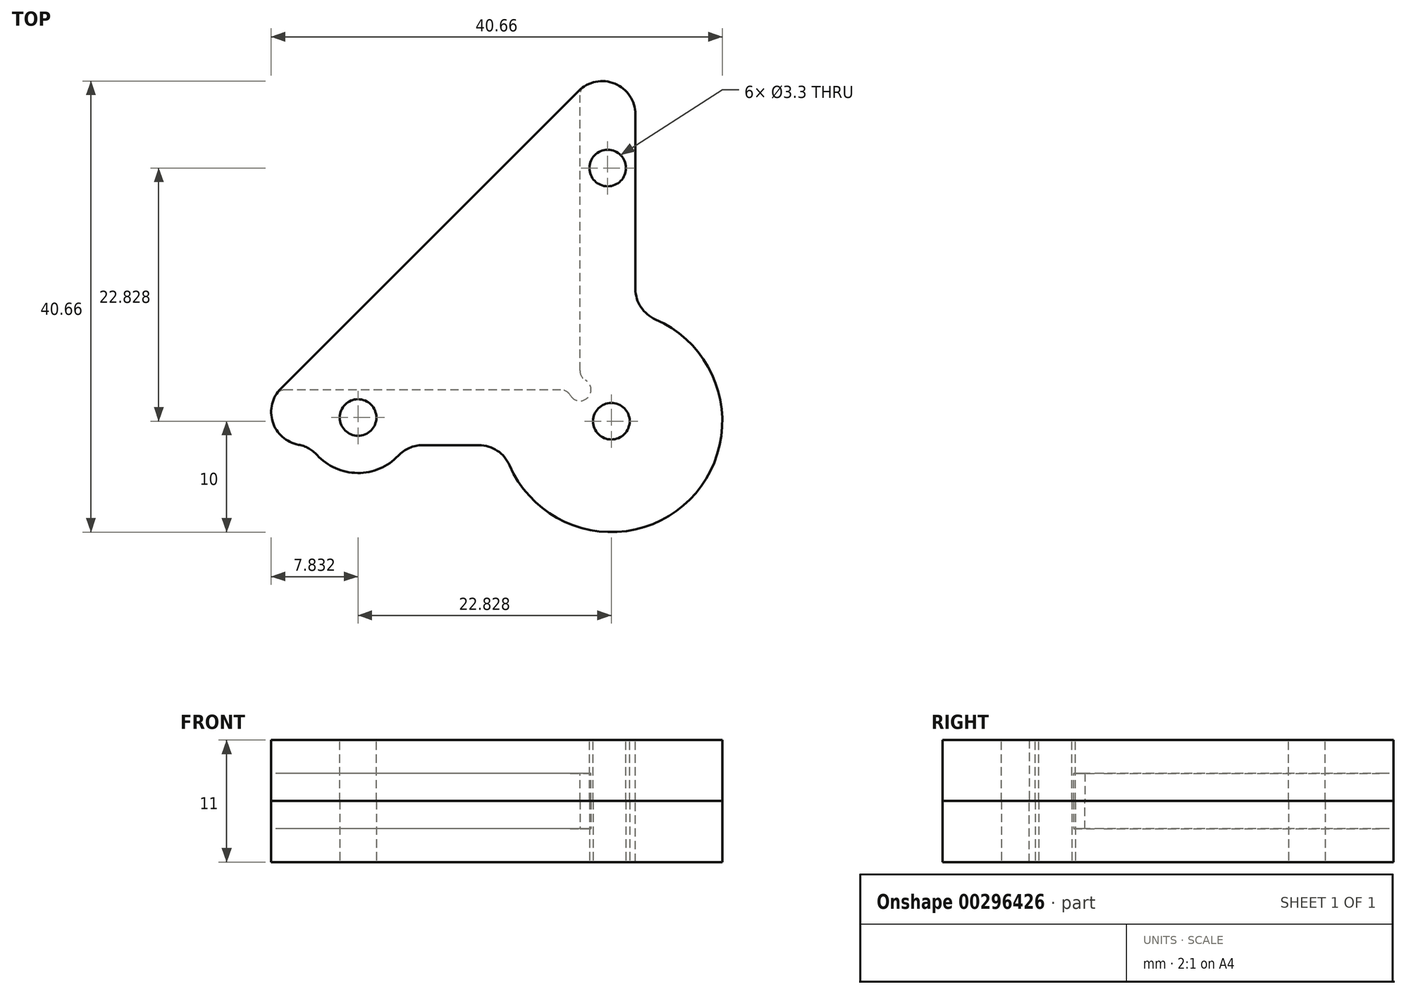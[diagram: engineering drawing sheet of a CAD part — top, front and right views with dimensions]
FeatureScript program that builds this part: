
annotation { "Feature Type Name" : "Feature", "Feature Type Description" : "" }
export const myFeature = defineFeature(function(context is Context, id is Id, definition is map)
    precondition{}
    {
        {
            var Q0;
            Q0=qCreatedBy(makeId("Top.planeOp"),FACE);
            var sketch = newSketch(context, id + "F0", { "sketchPlane" : qUnion([Q0])});
            skCircle(sketch, "E0", {"center": v(0, 0) * mm, "radius": 10 * mm});
            skCircle(sketch, "E1", {"center": v(0, 0) * mm, "radius": 1.65 * mm});
            skLineSegment(sketch, "E2", {"start": v(-2.83, 22.83) * mm, "end": v(2.17, 22.83) * mm, "construction": true});
            skLineSegment(sketch, "E3", {"start": v(-22.83, 2.83) * mm, "end": v(-22.83, -2.17) * mm, "construction": true});
            skPoint(sketch, "E4", {"position": v(-0.33, 22.83) * mm});
            skPoint(sketch, "E5", {"position": v(-22.83, 0.33) * mm});
            skCircle(sketch, "E6", {"center": v(-0.33, 22.83) * mm, "radius": 1.65 * mm});
            skCircle(sketch, "E7", {"center": v(-22.83, 0.33) * mm, "radius": 1.65 * mm});
            skLineSegment(sketch, "E8", {"start": v(0, 0) * mm, "end": v(-31.82, 31.82) * mm, "construction": true});
            skLineSegment(sketch, "E9", {"start": v(-2.83, 2.83) * mm, "end": v(-22.83, 2.83) * mm});
            skLineSegment(sketch, "E10", {"start": v(-2.83, 2.83) * mm, "end": v(-2.83, 22.83) * mm});
            skLineSegment(sketch, "E11", {"start": v(-22.83, 2.83) * mm, "end": v(-2.83, 22.83) * mm});
            skCircle(sketch, "E12", {"center": v(-2.83, 2.83) * mm, "radius": 1 * mm});
            skLineSegment(sketch, "E13", {"start": v(2.17, 9.76) * mm, "end": v(2.17, 34.9) * mm});
            skLineSegment(sketch, "E14", {"start": v(2.17, 34.9) * mm, "end": v(-34.9, -2.17) * mm});
            skLineSegment(sketch, "E15", {"start": v(-34.9, -2.17) * mm, "end": v(-9.76, -2.17) * mm});
            skLineSegment(sketch, "E16", {"start": v(-2.83, 22.83) * mm, "end": v(-2.83, 29.9) * mm});
            skLineSegment(sketch, "E17", {"start": v(-22.83, 2.83) * mm, "end": v(-29.9, 2.83) * mm});
            skArc(sketch, "E18", {"start": v(-27.16, -2.17) * mm, "mid": v(-22.83, -4.67) * mm, "end": v(-18.5, -2.17) * mm});
            skArc(sketch, "E19.MirrorCS", {"start": v(2.17, 27.16) * mm, "mid": v(4.67, 22.83) * mm, "end": v(2.17, 18.5) * mm});
            skSolve(sketch);
        }
        {
            var Q0;
            {var subQ5=sQuery(id+"F0.wireOp",EDGE,"Az8r9AQi-yTUi-chnx-iCbM-hz0Is2fI5o3N");Q0=makeQuery(id+"F0.imprint","IMPRINT",FACE,{"disambiguationData":[TD([[makeQuery(id+"F0.imprint","IMPRINT",EDGE,{"derivedFrom":subQ5}),-1.0]])]});}
            var Q1;
            Q1=makeQuery(id+"F0.imprint","IMPRINT",FACE,{"disambiguationData":[TD([[makeQuery(id+"F0.imprint","IMPRINT",EDGE,{"derivedFrom":sQuery(id+"F0.wireOp",EDGE,"Az8r9AQi-yTUi-chnx-iCbM-hz0Is2fI5o3N")}),1.0]])]});
            var Q2;
            {var subQ5=sQuery(id+"F0.wireOp",EDGE,"E11");Q2=makeQuery(id+"F0.imprint","IMPRINT",FACE,{"disambiguationData":[TD([[makeQuery(id+"F0.imprint","IMPRINT",EDGE,{"derivedFrom":subQ5}),-1.0]])]});}
            var Q3;
            {var subQ0=sQuery(id+"F0.wireOp",EDGE,"E10");var subQ1=sQuery(id+"F0.wireOp",EDGE,"E0");var subQ2=makeQuery(id+"F0.imprint","INTERSECT",VERTEX,{"derivedFrom":[subQ1,subQ0]});Q3=makeQuery(id+"F0.imprint","IMPRINT",FACE,{"disambiguationData":[TD([[makeQuery(id+"F0.imprint","IMPRINT",EDGE,{"disambiguationData":[TD([[subQ2,-1.0]])],"derivedFrom":subQ1}),1.0]])]});}
            var Q4;
            Q4=makeQuery(id+"F0.imprint","IMPRINT",FACE,{"disambiguationData":[TD([[makeQuery(id+"F0.imprint","IMPRINT",EDGE,{"derivedFrom":sQuery(id+"F0.wireOp",EDGE,"E11")}),1.0]])]});
            var Q5;
            {var subQ0=sQuery(id+"F0.wireOp",EDGE,"E10");var subQ1=sQuery(id+"F0.wireOp",EDGE,"E9");var subQ2=makeQuery(id+"F0.imprint","INTERSECT",VERTEX,{"derivedFrom":[subQ1,subQ0]});Q5=makeQuery(id+"F0.imprint","IMPRINT",FACE,{"disambiguationData":[TD([[makeQuery(id+"F0.imprint","IMPRINT",EDGE,{"disambiguationData":[TD([[subQ2,-1.0]])],"derivedFrom":subQ1}),1.0]])]});}
            var Q6;
            {var subQ0=sQuery(id+"F0.wireOp",EDGE,"E10");var subQ1=sQuery(id+"F0.wireOp",EDGE,"E9");var subQ2=makeQuery(id+"F0.imprint","INTERSECT",VERTEX,{"derivedFrom":[subQ1,subQ0]});Q6=makeQuery(id+"F0.imprint","IMPRINT",FACE,{"disambiguationData":[TD([[makeQuery(id+"F0.imprint","IMPRINT",EDGE,{"disambiguationData":[TD([[subQ2,-1.0]])],"derivedFrom":subQ1}),-1.0]])]});}
            extrude(context, id + "F1", {"entities" : qUnion([Q0, Q1, Q2, Q3, Q4, Q5, Q6]), "depth" : 3 * mm, "offsetDistance" : 25 * mm});
        }
        {
            var Q0;
            {var subQ0=sQuery(id+"F0.wireOp",EDGE,"seoE7kRg-yCuG-Cry2-NWf1-r5JpPazjEzeL");Q0=makeQuery(id+"F0.imprint","IMPRINT",FACE,{"disambiguationData":[TD([[makeQuery(id+"F0.imprint","IMPRINT",EDGE,{"derivedFrom":subQ0}),-1.0]])]});}
            var Q1;
            {var subQ0=sQuery(id+"F0.wireOp",EDGE,"cZFRohtI-Wnxx-kjr3-K0Pr-bqGsehvUnH0K");Q1=makeQuery(id+"F0.imprint","IMPRINT",FACE,{"disambiguationData":[TD([[makeQuery(id+"F0.imprint","IMPRINT",EDGE,{"derivedFrom":subQ0}),-1.0]])]});}
            var Q2;
            Q2=makeQuery(id+"F0.imprint","IMPRINT",FACE,{"disambiguationData":[TD([[makeQuery(id+"F0.imprint","IMPRINT",EDGE,{"derivedFrom":sQuery(id+"F0.wireOp",EDGE,"E1")}),-1.0]])]});
            var Q3;
            Q3=makeQuery(id+"F0.imprint","IMPRINT",FACE,{"disambiguationData":[TD([[makeQuery(id+"F0.imprint","IMPRINT",EDGE,{"derivedFrom":sQuery(id+"F0.wireOp",EDGE,"E6")}),-1.0]])]});
            var Q4;
            Q4=makeQuery(id+"F0.imprint","IMPRINT",FACE,{"disambiguationData":[TD([[makeQuery(id+"F0.imprint","IMPRINT",EDGE,{"derivedFrom":sQuery(id+"F0.wireOp",EDGE,"E7")}),-1.0]])]});
            var Q5;
            {var subQ0=sQuery(id+"F0.wireOp",EDGE,"E18");Q5=makeQuery(id+"F0.imprint","IMPRINT",FACE,{"disambiguationData":[TD([[makeQuery(id+"F0.imprint","IMPRINT",EDGE,{"derivedFrom":subQ0}),1.0]])]});}
            var Q6;
            {var subQ0=sQuery(id+"F0.wireOp",EDGE,"E19.MirrorCS");Q6=makeQuery(id+"F0.imprint","IMPRINT",FACE,{"disambiguationData":[TD([[makeQuery(id+"F0.imprint","IMPRINT",EDGE,{"derivedFrom":subQ0}),-1.0]])]});}
            extrude(context, id + "F2", {"entities" : qUnion([Q0, Q1, Q2, Q3, Q4, Q5, Q6]), "operationType" : NewBodyOperationType.ADD, "depth" : (3 + 2.5) * mm, "offsetDistance" : 25 * mm});
        }
        {
            var Q0;
            Q0=makeQuery(id+"F2.opExtrude","SWEPT_EDGE",EDGE,{"disambiguationData":[OSD([sQuery(id+"F0.wireOp",EDGE,"E13"),sQuery(id+"F0.wireOp",EDGE,"E14")])]});
            var Q1;
            Q1=makeQuery(id+"F2.opExtrude","SWEPT_EDGE",EDGE,{"disambiguationData":[OSD([sQuery(id+"F0.wireOp",EDGE,"E14"),sQuery(id+"F0.wireOp",EDGE,"E15")])]});
            fillet(context, id + "F3", {"entities" : qUnion([Q0, Q1]), "radius" : 3 * mm, "tangentPropagation" : true, "allowEdgeOverflow" : false});
        }
        {
            var Q0;
            {var subQ0=sQuery(id+"F0.wireOp",EDGE,"E0");var subQ1=sQuery(id+"F0.wireOp",EDGE,"cZFRohtI-Wnxx-kjr3-K0Pr-bqGsehvUnH0K");Q0=makeQuery(id+"F2.boolean.opBoolean","SPLIT",EDGE,{"disambiguationData":[topologyDisambiguationEdgeConnected([makeQuery(id+"F1.opExtrude","SWEPT_FACE",FACE,{"disambiguationData":[OSD([subQ0])]})])],"derivedFrom":makeQuery(id+"F2.opExtrude","SWEPT_EDGE",EDGE,{"disambiguationData":[OSD([subQ0,subQ1])]})});}
            var Q1;
            {var subQ0=sQuery(id+"F0.wireOp",EDGE,"E0");var subQ1=sQuery(id+"F0.wireOp",EDGE,"seoE7kRg-yCuG-Cry2-NWf1-r5JpPazjEzeL");Q1=makeQuery(id+"F2.boolean.opBoolean","SPLIT",EDGE,{"disambiguationData":[topologyDisambiguationEdgeConnected([makeQuery(id+"F1.opExtrude","SWEPT_FACE",FACE,{"disambiguationData":[OSD([subQ0])]})])],"derivedFrom":makeQuery(id+"F2.opExtrude","SWEPT_EDGE",EDGE,{"disambiguationData":[OSD([subQ0,subQ1])]})});}
            var Q2;
            {var subQ0=sQuery(id+"F0.wireOp",EDGE,"E18");var subQ1=sQuery(id+"F0.wireOp",EDGE,"E15");Q2=makeQuery(id+"F2.opExtrude","SWEPT_EDGE",EDGE,{"disambiguationData":[OSD([subQ1,subQ0]),TDD([makeQuery(id+"F0.imprint","INTERSECT",VERTEX,{"disambiguationData":[OD(1.0)],"derivedFrom":[subQ1,subQ0]})])]});}
            var Q3;
            {var subQ0=sQuery(id+"F0.wireOp",EDGE,"E18");var subQ1=sQuery(id+"F0.wireOp",EDGE,"E15");Q3=makeQuery(id+"F2.opExtrude","SWEPT_EDGE",EDGE,{"disambiguationData":[OSD([subQ1,subQ0]),TDD([makeQuery(id+"F0.imprint","INTERSECT",VERTEX,{"disambiguationData":[OD(0.0)],"derivedFrom":[subQ1,subQ0]})])]});}
            var Q4;
            {var subQ0=sQuery(id+"F0.wireOp",EDGE,"E19.MirrorCS");var subQ1=sQuery(id+"F0.wireOp",EDGE,"E13");Q4=makeQuery(id+"F2.opExtrude","SWEPT_EDGE",EDGE,{"disambiguationData":[OSD([subQ1,subQ0]),TDD([makeQuery(id+"F0.imprint","INTERSECT",VERTEX,{"disambiguationData":[OD(0.0)],"derivedFrom":[subQ1,subQ0]})])]});}
            var Q5;
            {var subQ0=sQuery(id+"F0.wireOp",EDGE,"E19.MirrorCS");var subQ1=sQuery(id+"F0.wireOp",EDGE,"E13");Q5=makeQuery(id+"F2.opExtrude","SWEPT_EDGE",EDGE,{"disambiguationData":[OSD([subQ1,subQ0]),TDD([makeQuery(id+"F0.imprint","INTERSECT",VERTEX,{"disambiguationData":[OD(1.0)],"derivedFrom":[subQ1,subQ0]})])]});}
            fillet(context, id + "F4", {"entities" : qUnion([Q0, Q1, Q2, Q3, Q4, Q5]), "radius" : 3 * mm, "tangentPropagation" : true, "allowEdgeOverflow" : false});
        }
        {
            var Q0;
            Q0=makeQuery(id+"F3.opFillet","BLEND_EDGE",EDGE,{"blendedFrom":[makeQuery(id+"F2.opExtrude","SWEPT_EDGE",EDGE,{"disambiguationData":[OSD([sQuery(id+"F0.wireOp",EDGE,"E13"),sQuery(id+"F0.wireOp",EDGE,"E14")])]}),makeQuery(id+"F2.opExtrude","SWEPT_FACE",FACE,{"disambiguationData":[OSD([sQuery(id+"F0.wireOp",EDGE,"E10"),sQuery(id+"F0.wireOp",EDGE,"E16")])]})],"blendedInto":[makeQuery(id+"F2.opExtrude","SWEPT_FACE",FACE,{"disambiguationData":[OSD([sQuery(id+"F0.wireOp",EDGE,"E10"),sQuery(id+"F0.wireOp",EDGE,"E16")])]})]});
            var Q1;
            Q1=makeQuery(id+"F3.opFillet","BLEND_EDGE",EDGE,{"blendedFrom":[makeQuery(id+"F2.opExtrude","SWEPT_EDGE",EDGE,{"disambiguationData":[OSD([sQuery(id+"F0.wireOp",EDGE,"E14"),sQuery(id+"F0.wireOp",EDGE,"E15")])]}),makeQuery(id+"F2.opExtrude","SWEPT_FACE",FACE,{"disambiguationData":[OSD([sQuery(id+"F0.wireOp",EDGE,"E9"),sQuery(id+"F0.wireOp",EDGE,"E17")])]})],"blendedInto":[makeQuery(id+"F2.opExtrude","SWEPT_FACE",FACE,{"disambiguationData":[OSD([sQuery(id+"F0.wireOp",EDGE,"E9"),sQuery(id+"F0.wireOp",EDGE,"E17")])]})]});
            var Q2;
            Q2=makeQuery(id+"F2.opExtrude","SWEPT_EDGE",EDGE,{"disambiguationData":[OSD([sQuery(id+"F0.wireOp",EDGE,"E10"),sQuery(id+"F0.wireOp",EDGE,"E12")])]});
            var Q3;
            Q3=makeQuery(id+"F2.opExtrude","SWEPT_EDGE",EDGE,{"disambiguationData":[OSD([sQuery(id+"F0.wireOp",EDGE,"E9"),sQuery(id+"F0.wireOp",EDGE,"E12")])]});
            fillet(context, id + "F5", {"entities" : qUnion([Q0, Q1, Q2, Q3]), "radius" : 1 * mm, "tangentPropagation" : true, "allowEdgeOverflow" : false});
        }
        {
            var Q0;
            Q0=makeQuery(id+"F1.opExtrude","SWEPT_BODY",BODY,{"disambiguationData":[OSD([sQuery(id+"F0.wireOp",EDGE,"E9"),sQuery(id+"F0.wireOp",EDGE,"E10"),sQuery(id+"F0.wireOp",EDGE,"E12"),sQuery(id+"F0.wireOp",EDGE,"E14"),sQuery(id+"F0.wireOp",EDGE,"E16"),sQuery(id+"F0.wireOp",EDGE,"E17")])]});
            var Q1;
            Q1=makeQuery(id+"F2.opExtrude","CAP_FACE",FACE,{"disambiguationData":[OSD([sQuery(id+"F0.wireOp",EDGE,"E0"),sQuery(id+"F0.wireOp",EDGE,"E1"),sQuery(id+"F0.wireOp",EDGE,"E6"),sQuery(id+"F0.wireOp",EDGE,"E7"),sQuery(id+"F0.wireOp",EDGE,"E9"),sQuery(id+"F0.wireOp",EDGE,"E10"),sQuery(id+"F0.wireOp",EDGE,"E12"),sQuery(id+"F0.wireOp",EDGE,"E13"),sQuery(id+"F0.wireOp",EDGE,"E14"),sQuery(id+"F0.wireOp",EDGE,"E15"),sQuery(id+"F0.wireOp",EDGE,"E16"),sQuery(id+"F0.wireOp",EDGE,"E17")])],"isStart":false});
            mirror(context, id + "F6", {"entities" : qUnion([Q0]), "mirrorPlane" : qUnion([Q1])});
        }
    });
